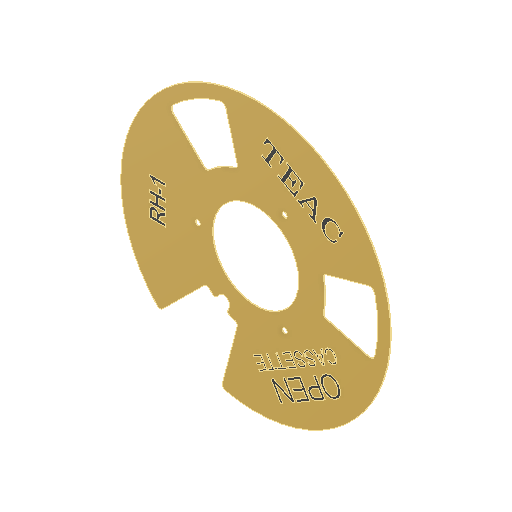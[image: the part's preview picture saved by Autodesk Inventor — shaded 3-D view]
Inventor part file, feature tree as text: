
AUTODESK INVENTOR PART (.ipt)
format: ipt  version: 2022 (Build 260153000, 153)  size: 641,536 bytes
history: native  units: mm
features: fillet x1
ambient origin geometry x8: Origin, YZ Plane, XZ Plane, XY Plane, X Axis, Y Axis, Z Axis, Center Point
bodies: Volumenkörper1 (feature_tree)
feature tree (1):
  fillet  "Fillet2"  [1 undecoded]
note: 1 required parameter value undecoded (feature->parameter linkage not recoverable at this tier; creation-order binding heuristic only, values carry confidence <= 0.55)
